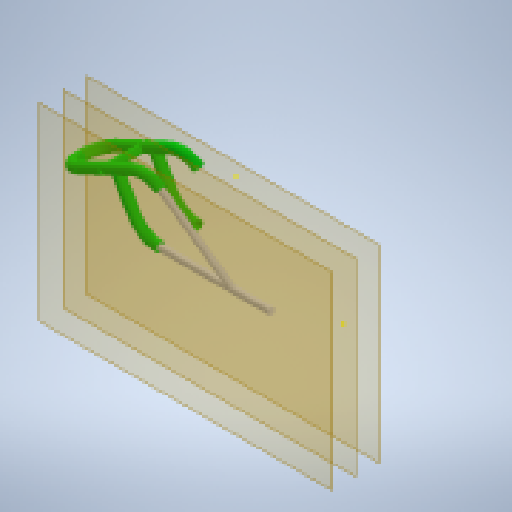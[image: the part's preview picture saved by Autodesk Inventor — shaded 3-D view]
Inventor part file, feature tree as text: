
AUTODESK INVENTOR PART (.ipt)
format: ipt  version: 2024 (Build 280153000, 153)  size: 404,992 bytes
history: native  units: in
note: dims shown in document units (in); Inventor stores cm internally (conversion verified against a paired STEP export)
features: other x11, sketch x5, plane x4
ambient origin geometry x8: Origin, YZ Plane, XZ Plane, XY Plane, X Axis, Y Axis, Z Axis, Center Point
bodies: Solid1 (feature_tree), Solid2 (feature_tree), Solid3 (feature_tree), Solid4 (feature_tree), Solid5 (feature_tree), Solid6 (feature_tree), Solid7 (feature_tree), Solid8 (feature_tree), Solid9 (feature_tree)
feature tree (20):
  other  "Link.ipt"
  other  "Solid1::Link.ipt"
  other  "Solid2::Link.ipt"
  other  "Solid3::Link.ipt"
  other  "Solid4::Link.ipt"
  other  "Solid5::Link.ipt"
  other  "Solid6::Link.ipt"
  other  "Solid7::Link.ipt"
  other  "Solid8::Link.ipt"
  other  "Solid9::Link.ipt"
  other  "TaggingFeature1"
  sketch  "Sketch1"  dims[d0=0.3937in]
  sketch  "Sketch2"
  sketch  "Sketch3"
  sketch  "Sketch4"
  sketch  "Sketch5"
  plane  "Work Plane1"
  plane  "Work Plane2"
  plane  "Work Plane3"
  plane  "Work Plane4"
